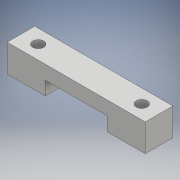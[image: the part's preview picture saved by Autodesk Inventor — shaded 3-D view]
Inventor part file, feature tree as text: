
AUTODESK INVENTOR PART (.ipt)
format: ipt  version: 2017 (Build 210142000, 142)  size: 113,152 bytes
history: native  units: mm
features: sketch x3, extrude x2, hole x1
ambient origin geometry x8: Origin, YZ Plane, XZ Plane, XY Plane, X Axis, Y Axis, Z Axis, Center Point
bodies: Solid1 (feature_tree)
feature tree (6):
  extrude  "Extrusion1"  Depth=4.0mm
  extrude  "Extrusion2"  Depth=9.0mm
  hole  "Hole1"  [1 undecoded]
  sketch  "Sketch1"  dims[d0=20.0mm d1=4.0mm]
  sketch  "Sketch2"  dims[d2=4.0mm d3=0.0mm d4=9.0mm]
  sketch  "Sketch3"  dims[d5=2.0mm d6=4.0mm d7=0.0mm d8=15.0mm d9=1.6mm d10=6.0mm d11=4.0mm d12=2.0mm d13=90.0deg d14=8.0mm d15=20.594885mm]
note: 1 required parameter value undecoded (feature->parameter linkage not recoverable at this tier; creation-order binding heuristic only, values carry confidence <= 0.55)
